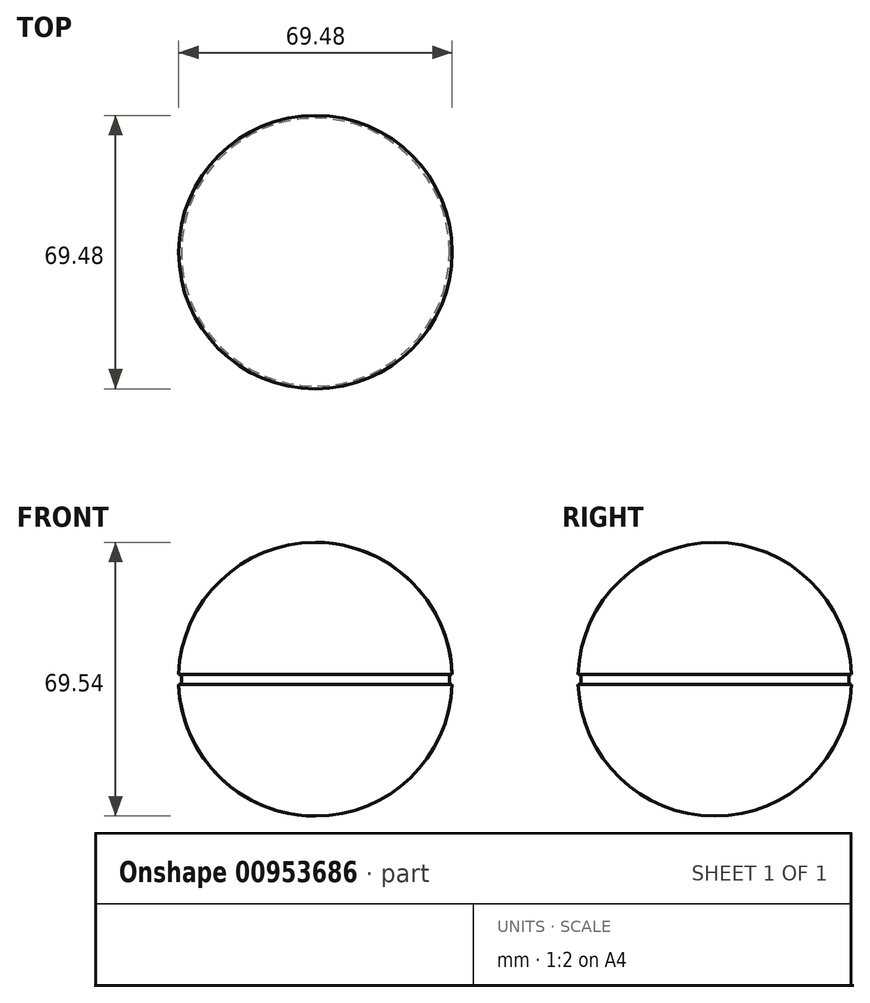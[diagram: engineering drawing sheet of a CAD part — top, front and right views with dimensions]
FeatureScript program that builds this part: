
annotation { "Feature Type Name" : "Feature", "Feature Type Description" : "" }
export const myFeature = defineFeature(function(context is Context, id is Id, definition is map)
    precondition{}
    {
        {
            var Q0;
            Q0=qCreatedBy(makeId("Front.planeOp"),FACE);
            var sketch = newSketch(context, id + "F0", { "sketchPlane" : qUnion([Q0])});
            skArc(sketch, "E0", {"start": v(0, -34.77) * mm, "mid": v(34.77, 0) * mm, "end": v(0, 34.77) * mm});
            skLineSegment(sketch, "E1", {"start": v(0, 34.77) * mm, "end": v(0, -34.77) * mm});
            skLineSegment(sketch, "E2.bottom", {"start": v(34.05, 1.27) * mm, "end": v(34.74, 1.27) * mm});
            skLineSegment(sketch, "E2.top", {"start": v(34.05, -1.27) * mm, "end": v(34.74, -1.27) * mm});
            skLineSegment(sketch, "E2.left", {"start": v(34.05, 1.27) * mm, "end": v(34.05, -1.27) * mm});
            skLineSegment(sketch, "E3", {"start": v(34.05, 0) * mm, "end": v(34.77, 0) * mm});
            skSolve(sketch);
        }
        {
            var Q0;
            Q0=makeQuery(id+"F0.imprint","IMPRINT",FACE,{"disambiguationData":[TD([[makeQuery(id+"F0.imprint","IMPRINT",EDGE,{"derivedFrom":sQuery(id+"F0.wireOp",EDGE,"E0")}),1.0]])]});
            var Q1;
            Q1=sQuery(id+"F0.wireOp",EDGE,"E1");
            revolve(context, id + "F1", {"surfaceOperationType" : NewSurfaceOperationType.NEW, "entities" : qUnion([Q0]), "axis" : qUnion([Q1]), "revolveType" : RevolveType.FULL});
        }
        {
            var Q0;
            Q0=qCreatedBy(makeId("Front.planeOp"),FACE);
            var sketch = newSketch(context, id + "F2", { "sketchPlane" : qUnion([Q0])});
            skArc(sketch, "E4", {"start": v(7.88, 1.27) * mm, "mid": v(0, 7.98) * mm, "end": v(-7.88, 1.27) * mm});
            skCircle(sketch, "E5", {"center": v(0, 0) * mm, "radius": 4.6 * mm});
            skLineSegment(sketch, "E6", {"start": v(-4.42, 1.27) * mm, "end": v(-7.88, 1.27) * mm});
            skLineSegment(sketch, "E7", {"start": v(-4.42, -1.27) * mm, "end": v(-7.88, -1.27) * mm});
            skLineSegment(sketch, "E8", {"start": v(7.88, 1.27) * mm, "end": v(4.42, 1.27) * mm});
            skLineSegment(sketch, "E9", {"start": v(4.42, -1.27) * mm, "end": v(7.88, -1.27) * mm});
            skArc(sketch, "E10.trimOffspring", {"start": v(-7.88, -1.27) * mm, "mid": v(0, -7.98) * mm, "end": v(7.88, -1.27) * mm});
            skSolve(sketch);
        }
        {
            var Q0;
            Q0=sQuery(id+"F2.wireOp",EDGE,"E5");
            var Q1;
            Q1=sQuery(id+"F2.wireOp",EDGE,"E4");
            var Q2;
            Q2=sQuery(id+"F2.wireOp",EDGE,"E10.trimOffspring");
            extrude(context, id + "F3", {"bodyType" : ToolBodyType.SURFACE, "operationType" : NewBodyOperationType.REMOVE, "surfaceEntities" : qUnion([Q0, Q1, Q2]), "depth" : 34.8 * mm, "offsetDistance" : 25.4 * mm});
        }
    });
